# Revit family: Domotics-DomesticRanges-GEWISS-CHORUS_CLIMATE-GAS_H2O_DETECTOR
name_source: partatom
category: Apparecchi elettrici
revit_build: Autodesk Revit 2016 (Build: 20161004_0715(x64)
units: mm (PartAtom-declared; Revit-internal decimal feet)

## family parameters
Condiviso = Sì
Host = Superficie
Mantenere orientamento annotazione = Sì
Punto di calcolo locali = Sì
Quota connettore circolare = Usa diametro
Taglio con vuoti quando caricato = Sì
Tipo di parte = Normale

## types (9) — shared parameters
Acqua = Sì
Catalogue = DOMOTICS
Catalogue Range = CHORUS - DOMESTIC RANGE
GPL = No
IDF = 025949b4-e392-4a13-bf96-e4b1bdb066ea
IDT = fd0c2516-d22c-4d53-a17f-e013153919b3
Immagine tipo = <Nessuno>
Metano = No
No. Chorus modules = 2
Offset_bidimensionale = 2 mm  [stored 0.00656168 ft]
Produttore = GEWISS S.p.A.
Prospetto di default = 1219 mm
Supply voltage = 12V ac/dc
Technical sheet = https://www.gewiss.com
Tipo_ = gas_acqua_g : GW14716 Rivelatore acqua 2M 12V titanio
URL = https://www.gewiss.com
Version file RFA = 19.0

## per-type parameters (varying)
| type | Colour | Description. | Descrizione | EAN code | Electrocod | Modello | No. Chorus modules: | SEO | Sensor | Tripping threshold |
| GW12712 - Detector ch4 2M 12V ac/dc black | Black | Methane detector | DETECTOR CH4 2M 12V AC/DC BLACK | 8011564267497 | 0531 | GW12712 | 2 | Detector | CH4 | 9% LIE |
| GW12711 - Lpg detector 2M 12V ac/dc black | Black | LPG detector | LPG DETECTOR 2M 12V AC/DC BLACK | 8011564267480 | 0531 | GW12711 | 2 | Detector | LPG | 9% LIE |
| GW14716 - Water detector, 2M 12V titanium | Titanium |  | WATER DETECTOR, 2M 12V TITANIUM |  |  | GW14716 |  |  | Water |  |
| GW12716 - Water detector 2M 12V black | Black |  | WATER DETECTOR 2M 12V BLACK |  |  | GW12716 |  |  | Water |  |
| GW14712 - Detector, ch4 2M 12V ac/dc titanium | Titanium | Methane detector | DETECTOR, CH4 2M 12V AC/DC TITANIUM | 8011564268739 | 0531 | GW14712 | 2 | Detector | CH4 | 9% LIE |
| GW14711 - Lpg detector, 2M 12V ac/dc titanium | Titanium | LPG detector | LPG DETECTOR, 2M 12V AC/DC TITANIUM | 8011564268722 | 0531 | GW14711 | 2 | Detector | LPG | 9% LIE |
| GW10712 - Ch4 detector 2M 12V ac/dc white | White | Methane detector | CH4 DETECTOR 2M 12V AC/DC WHITE | 8011564263154 | 0531 | GW10712 | 2 | Detector | CH4 | 9% LIE |
| GW10716 - Water detector, 2M 12V white | White |  | WATER DETECTOR, 2M 12V WHITE |  |  | GW10716 |  |  | Water |  |
| GW10711 - Lpg detector 2M 12V ac/dc white | White | LPG detector | LPG DETECTOR 2M 12V AC/DC WHITE | 8011564263130 | 0531 | GW10711 | 2 | Detector | LPG | 9% LIE |

note: [stored X ft] marks values corroborated as IEEE doubles in the binary element streams (Revit-internal decimal feet)

## geometry (parser evidence)
native form markers: Sweep x1
no freeform markers — native parametric forms only
